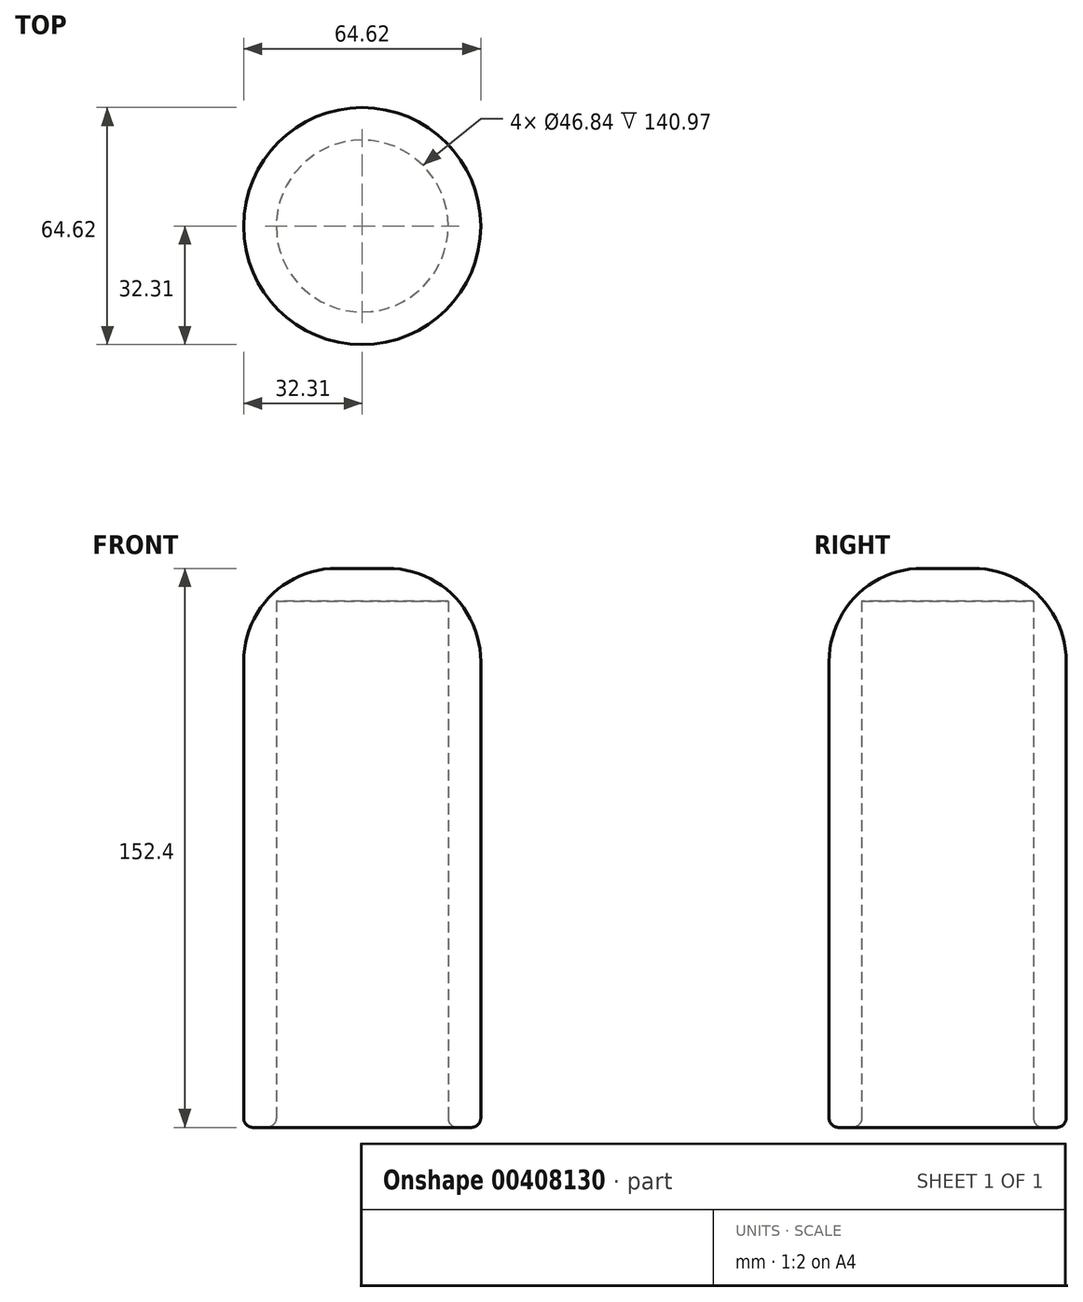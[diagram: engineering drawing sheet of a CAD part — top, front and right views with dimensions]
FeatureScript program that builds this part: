
annotation { "Feature Type Name" : "Feature", "Feature Type Description" : "" }
export const myFeature = defineFeature(function(context is Context, id is Id, definition is map)
    precondition{}
    {
        {
            var Q0;
            Q0=qCreatedBy(makeId("Top.planeOp"),FACE);
            var sketch = newSketch(context, id + "F0", { "sketchPlane" : qUnion([Q0])});
            skCircle(sketch, "E0", {"center": v(0, 0) * mm, "radius": 32.31 * mm});
            skSolve(sketch);
        }
        {
            var Q0;
            Q0=makeQuery(id+"F0.imprint","IMPRINT",FACE,{"disambiguationData":[TD([[makeQuery(id+"F0.imprint","IMPRINT",EDGE,{"derivedFrom":sQuery(id+"F0.wireOp",EDGE,"E0")}),1.0]])]});
            var Q1;
            Q1=sQuery(id+"F0.wireOp",EDGE,"E0");
            extrude(context, id + "F1", {"entities" : qUnion([Q0]), "surfaceEntities" : qUnion([Q1]), "depth" : 152.4 * mm});
        }
        {
            var Q0;
            Q0=makeQuery(id+"F1.opExtrude","CAP_FACE",FACE,{"disambiguationData":[OSD([sQuery(id+"F0.wireOp",EDGE,"E0")])],"isStart":true});
            shell(context, id + "F2", {"entities" : qUnion([Q0]), "thickness" : 8.9 * mm});
        }
        {
            var Q0;
            Q0=makeQuery(id+"F1.opExtrude","CAP_EDGE",EDGE,{"disambiguationData":[OSD([sQuery(id+"F0.wireOp",EDGE,"E0")])],"isStart":false});
            fillet(context, id + "F3", {"entities" : qUnion([Q0]), "radius" : 25.4 * mm, "tangentPropagation" : true, "allowEdgeOverflow" : false});
        }
        {
            var Q0;
            Q0=makeQuery(id+"F1.opExtrude","CAP_EDGE",EDGE,{"disambiguationData":[OSD([sQuery(id+"F0.wireOp",EDGE,"E0")])],"isStart":true});
            fillet(context, id + "F4", {"entities" : qUnion([Q0]), "radius" : 2.54 * mm, "tangentPropagation" : true, "allowEdgeOverflow" : false});
        }
        {
            var Q0;
            {var subQ0=sQuery(id+"F0.wireOp",EDGE,"E0");Q0=makeQuery(id+"F2.opShell","OFFSET_EDGE",EDGE,{"disambiguationData":[OSD([subQ0]),TDD([makeQuery(id+"F1.opExtrude","CAP_EDGE",EDGE,{"disambiguationData":[OSD([subQ0])],"isStart":true})])]});}
            fillet(context, id + "F5", {"entities" : qUnion([Q0]), "radius" : 2.54 * mm, "tangentPropagation" : true, "allowEdgeOverflow" : false});
        }
        {
            var Q0;
            Q0=makeQuery(id+"F1.opExtrude","SWEPT_BODY",BODY,{"disambiguationData":[OSD([sQuery(id+"F0.wireOp",EDGE,"E0")])]});
            var Q1;
            {var subQ0=sQuery(id+"F0.wireOp",EDGE,"E0");Q1=makeQuery(id+"F3.opFillet","BLEND_EDGE",EDGE,{"blendedFrom":[makeQuery(id+"F1.opExtrude","CAP_EDGE",EDGE,{"disambiguationData":[OSD([subQ0])],"isStart":false}),makeQuery(id+"F1.opExtrude","SWEPT_FACE",FACE,{"disambiguationData":[OSD([subQ0])]})],"blendedInto":[makeQuery(id+"F1.opExtrude","SWEPT_FACE",FACE,{"disambiguationData":[OSD([subQ0])]})]});}
            circularPattern(context, id + "F6", {"entities" : qUnion([Q0]), "axis" : qUnion([Q1]), "angle" : 360 * degree, "instanceCount" : 4, "equalSpace" : true});
        }
    });
